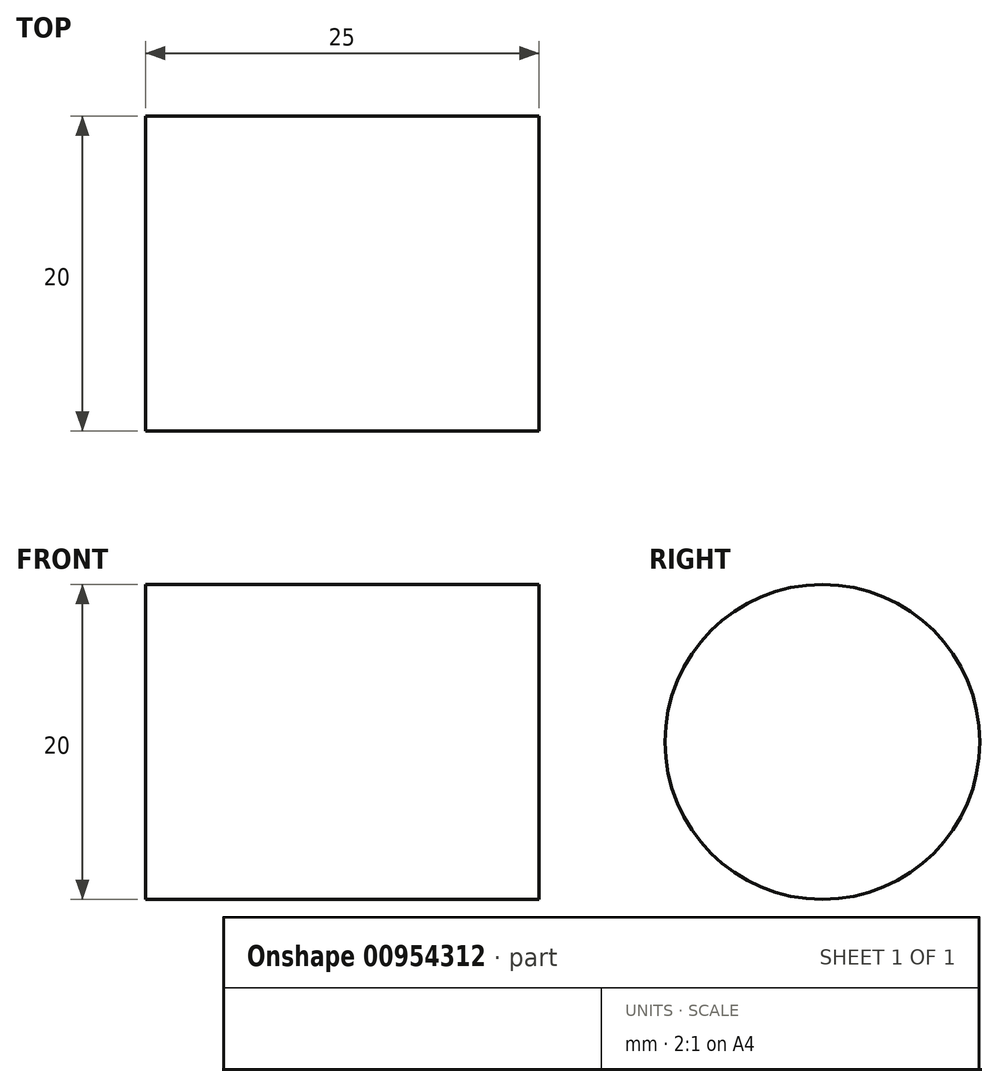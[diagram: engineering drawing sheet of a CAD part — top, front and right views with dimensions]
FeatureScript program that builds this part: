
annotation { "Feature Type Name" : "Feature", "Feature Type Description" : "" }
export const myFeature = defineFeature(function(context is Context, id is Id, definition is map)
    precondition{}
    {
        {
            var Q0;
            Q0=qCreatedBy(makeId("Top.planeOp"),FACE);
            var sketch = newSketch(context, id + "F0", { "sketchPlane" : qUnion([Q0])});
            skLineSegment(sketch, "E0", {"start": v(0, 0) * mm, "end": v(76.47, 0) * mm, "construction": true});
            skLineSegment(sketch, "E1", {"start": v(0, 0) * mm, "end": v(25, 0) * mm});
            skLineSegment(sketch, "E2", {"start": v(25, 0) * mm, "end": v(25, 10) * mm});
            skLineSegment(sketch, "E3", {"start": v(25, 10) * mm, "end": v(0, 10) * mm});
            skLineSegment(sketch, "E4", {"start": v(0, 10) * mm, "end": v(0, 0) * mm});
            skSolve(sketch);
        }
        {
            var Q0;
            Q0 = qSketchRegion(id + "F0", true);
            var Q1;
            Q1=sQuery(id+"F0.wireOp",EDGE,"E0");
            revolve(context, id + "F1", {"surfaceOperationType" : NewSurfaceOperationType.NEW, "entities" : qUnion([Q0]), "axis" : qUnion([Q1]), "revolveType" : RevolveType.FULL});
        }
    });
